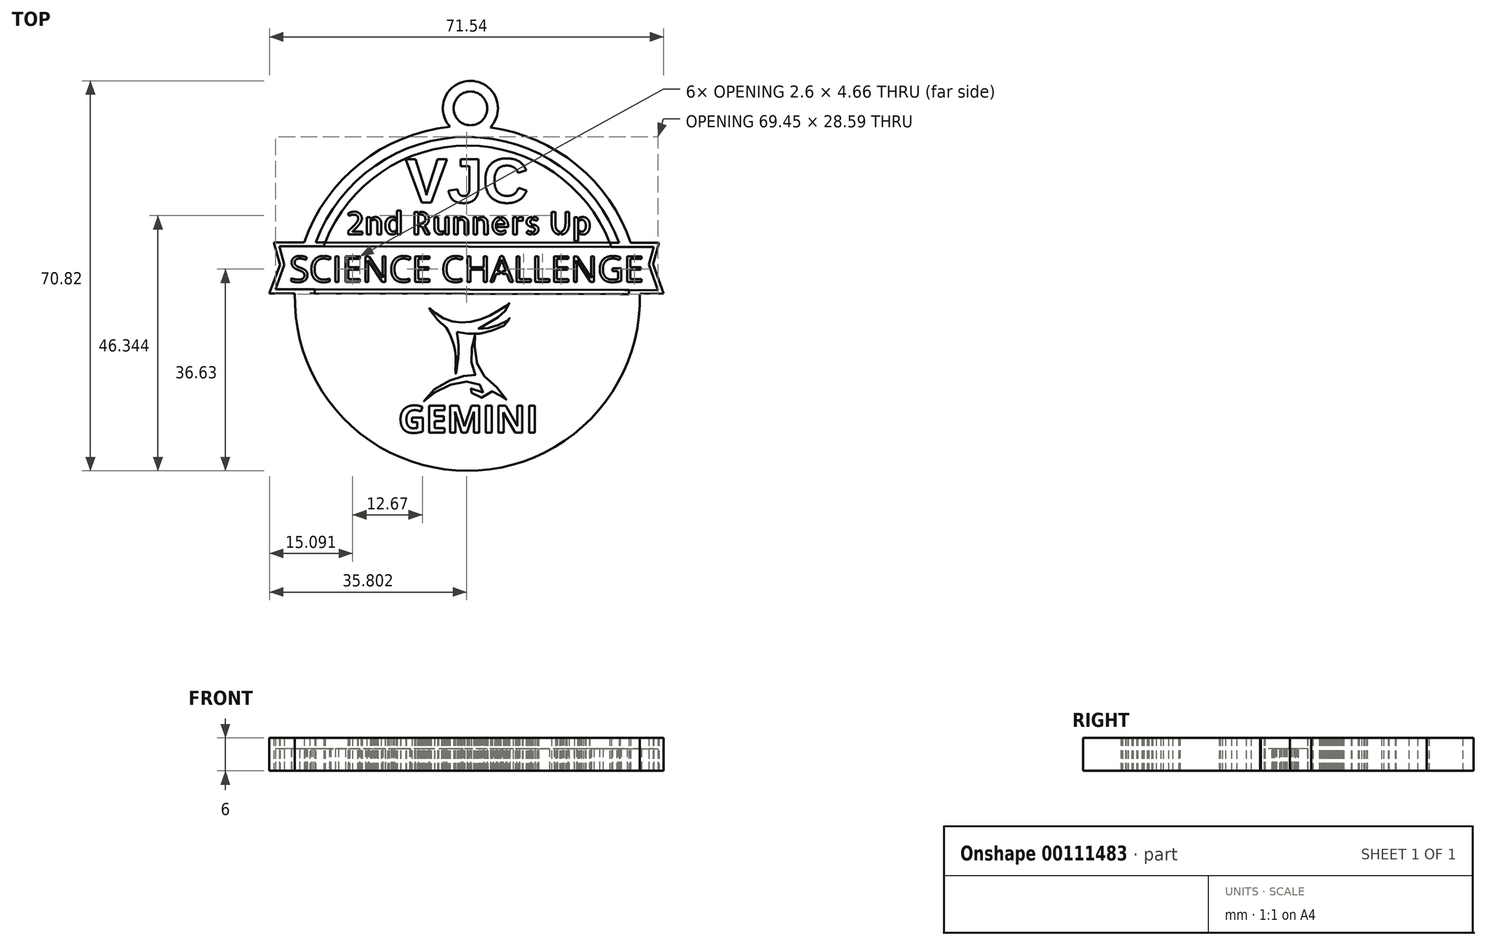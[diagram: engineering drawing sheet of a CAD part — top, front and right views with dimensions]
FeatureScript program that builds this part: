
annotation { "Feature Type Name" : "Feature", "Feature Type Description" : "" }
export const myFeature = defineFeature(function(context is Context, id is Id, definition is map)
    precondition{}
    {
        {
            var Q0;
            Q0=qCreatedBy(makeId("Top.planeOp"),FACE);
            var sketch = newSketch(context, id + "F0", { "sketchPlane" : qUnion([Q0])});
            skCircle(sketch, "E0", {"center": v(0.94, -3) * mm, "radius": 27.74 * mm});
            skPoint(sketch, "E0.first.point", {"position": v(1.58, 24.74) * mm});
            skPoint(sketch, "E0.second.point", {"position": v(0.52, -30.73) * mm});
            skPoint(sketch, "E0.third.point", {"position": v(-26.76, -1.33) * mm});
            skLineSegment(sketch, "E1", {"start": v(-24.87, 7.2) * mm, "end": v(-34.2, 7.2) * mm});
            skLineSegment(sketch, "E2", {"start": v(-34.2, 7.2) * mm, "end": v(-33.08, 3.11) * mm});
            skLineSegment(sketch, "E3", {"start": v(-33.08, 3.11) * mm, "end": v(-35, -2.1) * mm});
            skLineSegment(sketch, "E4", {"start": v(-35, -2.1) * mm, "end": v(-26.8, -2.1) * mm});
            skLineSegment(sketch, "E5", {"start": v(26.78, 7.1) * mm, "end": v(35.71, 7.1) * mm});
            skLineSegment(sketch, "E6", {"start": v(35.71, 7.1) * mm, "end": v(34.66, 3.21) * mm});
            skLineSegment(sketch, "E7", {"start": v(34.66, 3.21) * mm, "end": v(36.55, -2.1) * mm});
            skLineSegment(sketch, "E8", {"start": v(36.55, -2.1) * mm, "end": v(28.67, -2.25) * mm});
            skFitSpline(sketch, "E9", {"points": [v(-6, -4.72) * mm, v(-5.23, -5.35) * mm, v(-3.9, -6.35) * mm, v(-2.48, -6.98) * mm, v(-0.85, -7.35) * mm, v(0.35, -7.37) * mm, v(2.08, -7.15) * mm, v(3.86, -6.6) * mm, v(5.5, -5.84) * mm, v(6.83, -5.05) * mm, v(7.95, -4.34) * mm, v(8.2, -4.17) * mm, v(8.54, -3.89) * mm, v(8.14, -4.78) * mm, v(7.2, -5.82) * mm, v(5.2, -7.28) * mm, v(2.9, -8.45) * mm, v(3.98, -8.47) * mm, v(5.87, -8.12) * mm, v(7.76, -7.26) * mm, v(8.43, -6.75) * mm, v(8.6, -6.46) * mm, v(8.47, -7.15) * mm, v(6.46, -8.4) * mm, v(3.8, -9.28) * mm, v(1.11, -9.42) * mm, v(-0.95, -9.06) * mm], "startDerivative": vector(22.31, -18.25) * mm, "endDerivative": vector(-43, 9.84) * mm});
            skFitSpline(sketch, "E10", {"points": [v(-6, -4.72) * mm, v(-5.19, -6.01) * mm, v(-3.81, -7.48) * mm, v(-3.02, -8.2) * mm, v(-2.26, -9.47) * mm, v(-1.53, -11.45) * mm, v(-1.17, -13.95) * mm, v(-1.2, -16.67) * mm, v(-0.95, -15.45) * mm, v(-0.68, -11.98) * mm, v(-0.91, -9.36) * mm, v(-0.95, -9.06) * mm], "startDerivative": vector(8.3, -15) * mm, "endDerivative": vector(-0.86, 6) * mm});
            skFitSpline(sketch, "E11", {"points": [v(2.34, -9.66) * mm, v(2.02, -10.62) * mm, v(1.67, -12.76) * mm, v(1.67, -14.3) * mm, v(2.06, -16.19) * mm, v(2.36, -16.95) * mm, v(1.82, -16.92) * mm, v(-0.01, -17.17) * mm, v(-1.66, -17.64) * mm, v(-3.97, -18.79) * mm, v(-6.02, -20.44) * mm, v(-6.96, -21.68) * mm, v(-5.91, -20.77) * mm, v(-3.67, -19.33) * mm, v(-1.3, -18.4) * mm, v(0.83, -18.07) * mm, v(2.42, -18.3) * mm, v(3.7, -19.03) * mm, v(4.04, -19.68) * mm, v(3.45, -20.21) * mm, v(1.98, -19.81) * mm, v(1.3, -18.87) * mm, v(1.45, -19.8) * mm, v(2.36, -20.56) * mm, v(3.3, -21.02) * mm, v(4.84, -20.7) * mm, v(5.53, -19.8) * mm, v(6.38, -20.28) * mm, v(7.16, -20.84) * mm, v(8.14, -21.87) * mm, v(7.64, -20.68) * mm, v(6.28, -19.14) * mm, v(4.5, -17.53) * mm, v(3.33, -16.29) * mm, v(2.56, -14.18) * mm, v(2.24, -11.68) * mm, v(2.33, -10.24) * mm, v(2.34, -9.66) * mm]});
            skLineSegment(sketch, "E12", {"start": v(-24.87, 7.2) * mm, "end": v(28.1, 7.1) * mm});
            skLineSegment(sketch, "E13", {"start": v(-27.68, -2.1) * mm, "end": v(29.48, -2.24) * mm});
            skCircle(sketch, "E14.0", {"center": v(0.94, -3) * mm, "radius": 29.33 * mm});
            skCircle(sketch, "E15.0", {"center": v(0.94, -3) * mm, "radius": 31.31 * mm});
            skLineSegment(sketch, "E16.0", {"start": v(-24.87, 6.45) * mm, "end": v(28.1, 6.35) * mm});
            skLineSegment(sketch, "E17.0", {"start": v(-24.87, 6.45) * mm, "end": v(-33.21, 6.45) * mm});
            skLineSegment(sketch, "E18", {"start": v(28.1, 6.35) * mm, "end": v(34.73, 6.35) * mm});
            skLineSegment(sketch, "E19.0", {"start": v(-27.68, -1.35) * mm, "end": v(29.48, -1.49) * mm});
            skLineSegment(sketch, "E20", {"start": v(-27.68, -1.35) * mm, "end": v(-33.91, -1.33) * mm});
            skLineSegment(sketch, "E21", {"start": v(29.48, -1.49) * mm, "end": v(35.54, -1.5) * mm});
            skLineSegment(sketch, "E22.0", {"start": v(34.73, 6.35) * mm, "end": v(33.88, 3.18) * mm});
            skLineSegment(sketch, "E23.0", {"start": v(33.88, 3.18) * mm, "end": v(35.54, -1.5) * mm});
            skLineSegment(sketch, "E24.0", {"start": v(-32.3, 3.08) * mm, "end": v(-33.91, -1.33) * mm});
            skLineSegment(sketch, "E25.trimOffspring", {"start": v(-33.21, 6.45) * mm, "end": v(-32.3, 3.08) * mm});
            skText(sketch, "E26", { "text": "SCIENCE CHALLENGE", "fontName": "OpenSans-Regular.ttf"});
            skText(sketch, "E27", { "text": "GEMINI", "fontName": "OpenSans-Bold.ttf"});
            skText(sketch, "E28", { "text": "VJC", "fontName": "Arimo-Bold.ttf"});
            skLineSegment(sketch, "E29", {"start": v(6.9, 1.33) * mm, "end": v(6.9, 2.22) * mm});
            skLineSegment(sketch, "E30", {"start": v(6.9, 2.22) * mm, "end": v(7.18, 2.22) * mm});
            skLineSegment(sketch, "E31", {"start": v(7.18, 2.22) * mm, "end": v(7.26, 2.22) * mm});
            skLineSegment(sketch, "E32", {"start": v(7.26, 2.22) * mm, "end": v(7.26, 1.34) * mm});
            skLineSegment(sketch, "E33", {"start": v(7.26, 1.34) * mm, "end": v(6.9, 1.33) * mm});
            skCircle(sketch, "E34", {"center": v(1.48, 31.52) * mm, "radius": 3.06 * mm});
            skCircle(sketch, "E35.0", {"center": v(1.48, 31.52) * mm, "radius": 5 * mm});
            skText(sketch, "E36", { "text": "2nd Runners Up", "fontName": "AllertaStencil-Regular.ttf"});
            const initialGuessF0  = {"E26": [-0.03136, 0, 1, 0, 0.0047], "E27": [-0.0116, -0.02738, 1, 0, 0.00494], "E28": [-0.01032, 0.01442, 1, 0, 0.00826], "E36": [-0.02119, 0.00863, 1, 0, 0.0041]};
            skSetInitialGuess(sketch, initialGuessF0);
            skSolve(sketch);
        }
        {
            var Q0;
            Q0=makeQuery(id+"F0.imprint","IMPRINT",FACE,{"disambiguationData":[TD([[makeQuery(id+"F0.imprint","IMPRINT",EDGE,{"derivedFrom":sQuery(id+"F0.wireOp",EDGE,"f2c7ee9f-897c-4c1d-89b3-a48ac7c6bfa7.sketch_text.stroke-0")}),1.0]])]});
            var Q1;
            {var subQ0=sQuery(id+"F0.wireOp",EDGE,"E15.0");var subQ1=sQuery(id+"F0.wireOp",EDGE,"E1");var subQ2=makeQuery(id+"F0.imprint","INTERSECT",VERTEX,{"derivedFrom":[subQ1,subQ0]});Q1=makeQuery(id+"F0.imprint","IMPRINT",FACE,{"disambiguationData":[TD([[makeQuery(id+"F0.imprint","IMPRINT",EDGE,{"disambiguationData":[TD([[subQ2,1.0]])],"derivedFrom":subQ1}),-1.0]])]});}
            var Q2;
            Q2=makeQuery(id+"F0.imprint","IMPRINT",FACE,{"disambiguationData":[TD([[makeQuery(id+"F0.imprint","IMPRINT",EDGE,{"derivedFrom":sQuery(id+"F0.wireOp",EDGE,"26462852-2f77-49b2-9a3d-6dfd93b606f1.sketch_text.stroke-0")}),1.0]])]});
            var Q3;
            {var subQ0=sQuery(id+"F0.wireOp",EDGE,"E15.0");var subQ1=sQuery(id+"F0.wireOp",EDGE,"E4");var subQ2=makeQuery(id+"F0.imprint","INTERSECT",VERTEX,{"derivedFrom":[subQ1,subQ0]});Q3=makeQuery(id+"F0.imprint","IMPRINT",FACE,{"disambiguationData":[TD([[makeQuery(id+"F0.imprint","IMPRINT",EDGE,{"disambiguationData":[TD([[subQ2,-1.0]])],"derivedFrom":subQ1}),-1.0]])]});}
            var Q4;
            {var subQ7=sQuery(id+"F0.wireOp",EDGE,"E2");Q4=makeQuery(id+"F0.imprint","IMPRINT",FACE,{"disambiguationData":[TD([[makeQuery(id+"F0.imprint","IMPRINT",EDGE,{"derivedFrom":subQ7}),1.0]])]});}
            var Q5;
            {var subQ3=sQuery(id+"F0.wireOp",EDGE,"E17.0");var subQ10=makeQuery(id+"F0.imprint","IMPRINT",VERTEX,{"derivedFrom":subQ3});Q5=makeQuery(id+"F0.imprint","IMPRINT",FACE,{"disambiguationData":[TD([[makeQuery(id+"F0.imprint","IMPRINT",EDGE,{"disambiguationData":[TD([[subQ10,1.0]])],"derivedFrom":subQ3}),-1.0]])]});}
            var Q6;
            {var subQ0=sQuery(id+"F0.wireOp",EDGE,"E1");var subQ5=sQuery(id+"F0.wireOp",EDGE,"E14.0");var subQ6=makeQuery(id+"F0.imprint","INTERSECT",VERTEX,{"derivedFrom":[subQ0,subQ5]});Q6=makeQuery(id+"F0.imprint","IMPRINT",FACE,{"disambiguationData":[TD([[makeQuery(id+"F0.imprint","IMPRINT",EDGE,{"disambiguationData":[TD([[subQ6,-1.0]])],"derivedFrom":subQ5}),1.0]])]});}
            var Q7;
            {var subQ1=sQuery(id+"F0.wireOp",EDGE,"E5");var subQ6=sQuery(id+"F0.wireOp",EDGE,"E0");var subQ7=makeQuery(id+"F0.imprint","INTERSECT",VERTEX,{"derivedFrom":[subQ6,subQ1]});Q7=makeQuery(id+"F0.imprint","IMPRINT",FACE,{"disambiguationData":[TD([[makeQuery(id+"F0.imprint","IMPRINT",EDGE,{"disambiguationData":[TD([[subQ7,1.0]])],"derivedFrom":subQ6}),-1.0]])]});}
            var Q8;
            {var subQ0=sQuery(id+"F0.wireOp",EDGE,"E15.0");var subQ1=sQuery(id+"F0.wireOp",EDGE,"E5");var subQ2=makeQuery(id+"F0.imprint","INTERSECT",VERTEX,{"derivedFrom":[subQ1,subQ0]});Q8=makeQuery(id+"F0.imprint","IMPRINT",FACE,{"disambiguationData":[TD([[makeQuery(id+"F0.imprint","IMPRINT",EDGE,{"disambiguationData":[TD([[subQ2,1.0]])],"derivedFrom":subQ1}),-1.0]])]});}
            var Q9;
            {var subQ11=sQuery(id+"F0.wireOp",EDGE,"E6");Q9=makeQuery(id+"F0.imprint","IMPRINT",FACE,{"disambiguationData":[TD([[makeQuery(id+"F0.imprint","IMPRINT",EDGE,{"derivedFrom":subQ11}),-1.0]])]});}
            var Q10;
            {var subQ0=sQuery(id+"F0.wireOp",EDGE,"E13");var subQ1=sQuery(id+"F0.wireOp",EDGE,"E0");var subQ2=makeQuery(id+"F0.imprint","INTERSECT",VERTEX,{"disambiguationData":[OD(0.0)],"derivedFrom":[subQ1,subQ0]});Q10=makeQuery(id+"F0.imprint","IMPRINT",FACE,{"disambiguationData":[TD([[makeQuery(id+"F0.imprint","IMPRINT",EDGE,{"disambiguationData":[TD([[subQ2,-1.0]])],"derivedFrom":subQ1}),1.0]])]});}
            var Q11;
            {var subQ0=sQuery(id+"F0.wireOp",EDGE,"E13");var subQ3=sQuery(id+"F0.wireOp",EDGE,"E0");var subQ4=makeQuery(id+"F0.imprint","INTERSECT",VERTEX,{"disambiguationData":[OD(0.0)],"derivedFrom":[subQ3,subQ0]});Q11=makeQuery(id+"F0.imprint","IMPRINT",FACE,{"disambiguationData":[TD([[makeQuery(id+"F0.imprint","IMPRINT",EDGE,{"disambiguationData":[TD([[subQ4,-1.0]])],"derivedFrom":subQ3}),-1.0]])]});}
            var Q12;
            {var subQ0=sQuery(id+"F0.wireOp",EDGE,"E15.0");var subQ1=sQuery(id+"F0.wireOp",EDGE,"E8");var subQ2=makeQuery(id+"F0.imprint","INTERSECT",VERTEX,{"derivedFrom":[subQ1,subQ0]});Q12=makeQuery(id+"F0.imprint","IMPRINT",FACE,{"disambiguationData":[TD([[makeQuery(id+"F0.imprint","IMPRINT",EDGE,{"disambiguationData":[TD([[subQ2,-1.0]])],"derivedFrom":subQ1}),-1.0]])]});}
            var Q13;
            {var subQ0=sQuery(id+"F0.wireOp",EDGE,"E15.0");var subQ1=sQuery(id+"F0.wireOp",EDGE,"E1");var subQ2=makeQuery(id+"F0.imprint","INTERSECT",VERTEX,{"derivedFrom":[subQ1,subQ0]});Q13=makeQuery(id+"F0.imprint","IMPRINT",FACE,{"disambiguationData":[TD([[makeQuery(id+"F0.imprint","IMPRINT",EDGE,{"disambiguationData":[TD([[subQ2,1.0]])],"derivedFrom":subQ1}),1.0]])]});}
            var Q14;
            {var subQ0=sQuery(id+"F0.wireOp",EDGE,"E15.0");var subQ1=sQuery(id+"F0.wireOp",EDGE,"E4");var subQ2=makeQuery(id+"F0.imprint","INTERSECT",VERTEX,{"derivedFrom":[subQ1,subQ0]});Q14=makeQuery(id+"F0.imprint","IMPRINT",FACE,{"disambiguationData":[TD([[makeQuery(id+"F0.imprint","IMPRINT",EDGE,{"disambiguationData":[TD([[subQ2,-1.0]])],"derivedFrom":subQ1}),1.0]])]});}
            var Q15;
            {var subQ0=sQuery(id+"F0.wireOp",EDGE,"E4");var subQ1=sQuery(id+"F0.wireOp",EDGE,"E0");var subQ2=makeQuery(id+"F0.imprint","INTERSECT",VERTEX,{"derivedFrom":[subQ1,subQ0]});Q15=makeQuery(id+"F0.imprint","IMPRINT",FACE,{"disambiguationData":[TD([[makeQuery(id+"F0.imprint","IMPRINT",EDGE,{"disambiguationData":[TD([[subQ2,1.0]])],"derivedFrom":subQ1}),-1.0]])]});}
            var Q16;
            Q16=makeQuery(id+"F0.imprint","IMPRINT",FACE,{"disambiguationData":[TD([[makeQuery(id+"F0.imprint","IMPRINT",EDGE,{"derivedFrom":sQuery(id+"F0.wireOp",EDGE,"E9")}),1.0]])]});
            var Q17;
            {var subQ0=sQuery(id+"F0.wireOp",EDGE,"E35.0");var subQ1=sQuery(id+"F0.wireOp",EDGE,"E15.0");var subQ2=makeQuery(id+"F0.imprint","INTERSECT",VERTEX,{"disambiguationData":[OD(0.0)],"derivedFrom":[subQ1,subQ0]});Q17=makeQuery(id+"F0.imprint","IMPRINT",FACE,{"disambiguationData":[TD([[makeQuery(id+"F0.imprint","IMPRINT",EDGE,{"disambiguationData":[TD([[subQ2,-1.0]])],"derivedFrom":subQ1}),-1.0]])]});}
            var Q18;
            {var subQ0=sQuery(id+"F0.wireOp",EDGE,"E35.0");var subQ1=sQuery(id+"F0.wireOp",EDGE,"E15.0");var subQ2=makeQuery(id+"F0.imprint","INTERSECT",VERTEX,{"disambiguationData":[OD(0.0)],"derivedFrom":[subQ1,subQ0]});Q18=makeQuery(id+"F0.imprint","IMPRINT",FACE,{"disambiguationData":[TD([[makeQuery(id+"F0.imprint","IMPRINT",EDGE,{"disambiguationData":[TD([[subQ2,-1.0]])],"derivedFrom":subQ1}),1.0]])]});}
            var Q19;
            Q19=makeQuery(id+"F0.imprint","IMPRINT",FACE,{"disambiguationData":[TD([[makeQuery(id+"F0.imprint","IMPRINT",EDGE,{"derivedFrom":sQuery(id+"F0.wireOp",EDGE,"E28.sketch_text.stroke-0")}),1.0]])]});
            extrude(context, id + "F1", {"entities" : qUnion([Q0, Q1, Q2, Q3, Q4, Q5, Q6, Q7, Q8, Q9, Q10, Q11, Q12, Q13, Q14, Q15, Q16, Q17, Q18, Q19]), "depth" : 6 * mm});
        }
        {
            var Q0;
            {var subQ0=sQuery(id+"F0.wireOp",EDGE,"E24.0");Q0=makeQuery(id+"F0.imprint","IMPRINT",FACE,{"disambiguationData":[TD([[makeQuery(id+"F0.imprint","IMPRINT",EDGE,{"derivedFrom":subQ0}),1.0]])]});}
            var Q1;
            {var subQ11=sQuery(id+"F0.wireOp",EDGE,"E26.sketch_text.stroke-16");Q1=makeQuery(id+"F0.imprint","IMPRINT",FACE,{"disambiguationData":[TD([[makeQuery(id+"F0.imprint","IMPRINT",EDGE,{"derivedFrom":subQ11}),1.0]])]});}
            var Q2;
            {var subQ0=sQuery(id+"F0.wireOp",EDGE,"E26.sketch_text.stroke-33");Q2=makeQuery(id+"F0.imprint","IMPRINT",FACE,{"disambiguationData":[TD([[makeQuery(id+"F0.imprint","IMPRINT",EDGE,{"derivedFrom":subQ0}),1.0]])]});}
            var Q3;
            {var subQ10=sQuery(id+"F0.wireOp",EDGE,"E26.sketch_text.stroke-28");Q3=makeQuery(id+"F0.imprint","IMPRINT",FACE,{"disambiguationData":[TD([[makeQuery(id+"F0.imprint","IMPRINT",EDGE,{"derivedFrom":subQ10}),1.0]])]});}
            var Q4;
            {var subQ25=sQuery(id+"F0.wireOp",EDGE,"E26.sketch_text.stroke-178");Q4=makeQuery(id+"F0.imprint","IMPRINT",FACE,{"disambiguationData":[TD([[makeQuery(id+"F0.imprint","IMPRINT",EDGE,{"derivedFrom":subQ25}),1.0]])]});}
            var Q5;
            {var subQ1=sQuery(id+"F0.wireOp",EDGE,"E26.sketch_text.stroke-198");var subQ3=sQuery(id+"F0.wireOp",EDGE,"E14.0");var subQ4=makeQuery(id+"F0.imprint","INTERSECT",VERTEX,{"derivedFrom":[subQ3,subQ1]});Q5=makeQuery(id+"F0.imprint","IMPRINT",FACE,{"disambiguationData":[TD([[makeQuery(id+"F0.imprint","IMPRINT",EDGE,{"disambiguationData":[TD([[subQ4,-1.0]])],"derivedFrom":subQ3}),-1.0]])]});}
            var Q6;
            {var subQ8=sQuery(id+"F0.wireOp",EDGE,"E22.0");Q6=makeQuery(id+"F0.imprint","IMPRINT",FACE,{"disambiguationData":[TD([[makeQuery(id+"F0.imprint","IMPRINT",EDGE,{"derivedFrom":subQ8}),-1.0]])]});}
            var Q7;
            {var subQ0=sQuery(id+"F0.wireOp",EDGE,"E26.sketch_text.stroke-6");Q7=makeQuery(id+"F0.imprint","IMPRINT",FACE,{"disambiguationData":[TD([[makeQuery(id+"F0.imprint","IMPRINT",EDGE,{"derivedFrom":subQ0}),1.0]])]});}
            var Q8;
            {var subQ6=sQuery(id+"F0.wireOp",EDGE,"E26.sketch_text.stroke-1");Q8=makeQuery(id+"F0.imprint","IMPRINT",FACE,{"disambiguationData":[TD([[makeQuery(id+"F0.imprint","IMPRINT",EDGE,{"derivedFrom":subQ6}),1.0]])]});}
            var Q9;
            {var subQ6=sQuery(id+"F0.wireOp",EDGE,"E26.sketch_text.stroke-189");Q9=makeQuery(id+"F0.imprint","IMPRINT",FACE,{"disambiguationData":[TD([[makeQuery(id+"F0.imprint","IMPRINT",EDGE,{"derivedFrom":subQ6}),1.0]])]});}
            var Q10;
            {var subQ5=sQuery(id+"F0.wireOp",EDGE,"E26.sketch_text.stroke-202");Q10=makeQuery(id+"F0.imprint","IMPRINT",FACE,{"disambiguationData":[TD([[makeQuery(id+"F0.imprint","IMPRINT",EDGE,{"derivedFrom":subQ5}),1.0]])]});}
            var Q11;
            {var subQ5=sQuery(id+"F0.wireOp",EDGE,"E26.sketch_text.stroke-206");Q11=makeQuery(id+"F0.imprint","IMPRINT",FACE,{"disambiguationData":[TD([[makeQuery(id+"F0.imprint","IMPRINT",EDGE,{"derivedFrom":subQ5}),1.0]])]});}
            var Q12;
            {var subQ0=sQuery(id+"F0.wireOp",EDGE,"E21");var subQ1=sQuery(id+"F0.wireOp",EDGE,"E14.0");var subQ2=makeQuery(id+"F0.imprint","INTERSECT",VERTEX,{"derivedFrom":[subQ1,subQ0]});Q12=makeQuery(id+"F0.imprint","IMPRINT",FACE,{"disambiguationData":[TD([[makeQuery(id+"F0.imprint","IMPRINT",EDGE,{"disambiguationData":[TD([[subQ2,-1.0]])],"derivedFrom":subQ1}),-1.0]])]});}
            var Q13;
            Q13=makeQuery(id+"F0.imprint","IMPRINT",FACE,{"disambiguationData":[TD([[makeQuery(id+"F0.imprint","IMPRINT",EDGE,{"derivedFrom":sQuery(id+"F0.wireOp",EDGE,"E26.sketch_text.stroke-133")}),1.0]])]});
            var Q14;
            {var subQ5=sQuery(id+"F0.wireOp",EDGE,"E26.sketch_text.stroke-26");Q14=makeQuery(id+"F0.imprint","IMPRINT",FACE,{"disambiguationData":[TD([[makeQuery(id+"F0.imprint","IMPRINT",EDGE,{"derivedFrom":subQ5}),1.0]])]});}
            var Q15;
            {var subQ1=sQuery(id+"F0.wireOp",EDGE,"E26.sketch_text.stroke-19");Q15=makeQuery(id+"F0.imprint","IMPRINT",FACE,{"disambiguationData":[TD([[makeQuery(id+"F0.imprint","IMPRINT",EDGE,{"derivedFrom":subQ1}),1.0]])]});}
            var Q16;
            {var subQ5=sQuery(id+"F0.wireOp",EDGE,"E33");Q16=makeQuery(id+"F0.imprint","IMPRINT",FACE,{"disambiguationData":[TD([[makeQuery(id+"F0.imprint","IMPRINT",EDGE,{"derivedFrom":subQ5}),-1.0]])]});}
            var Q17;
            {var subQ0=sQuery(id+"F0.wireOp",EDGE,"E32");var subQ1=sQuery(id+"F0.wireOp",EDGE,"E26.sketch_text.stroke-126");var subQ2=makeQuery(id+"F0.imprint","INTERSECT",VERTEX,{"derivedFrom":[subQ1,subQ0]});Q17=makeQuery(id+"F0.imprint","IMPRINT",FACE,{"disambiguationData":[TD([[makeQuery(id+"F0.imprint","IMPRINT",EDGE,{"disambiguationData":[TD([[subQ2,-1.0]])],"derivedFrom":subQ1}),-1.0]])]});}
            var Q18;
            {var subQ1=sQuery(id+"F0.wireOp",EDGE,"E30");Q18=makeQuery(id+"F0.imprint","IMPRINT",FACE,{"disambiguationData":[TD([[makeQuery(id+"F0.imprint","IMPRINT",EDGE,{"derivedFrom":subQ1}),-1.0]])]});}
            extrude(context, id + "F2", {"entities" : qUnion([Q0, Q1, Q2, Q3, Q4, Q5, Q6, Q7, Q8, Q9, Q10, Q11, Q12, Q13, Q14, Q15, Q16, Q17, Q18]), "depth" : 4 * mm});
        }
    });
